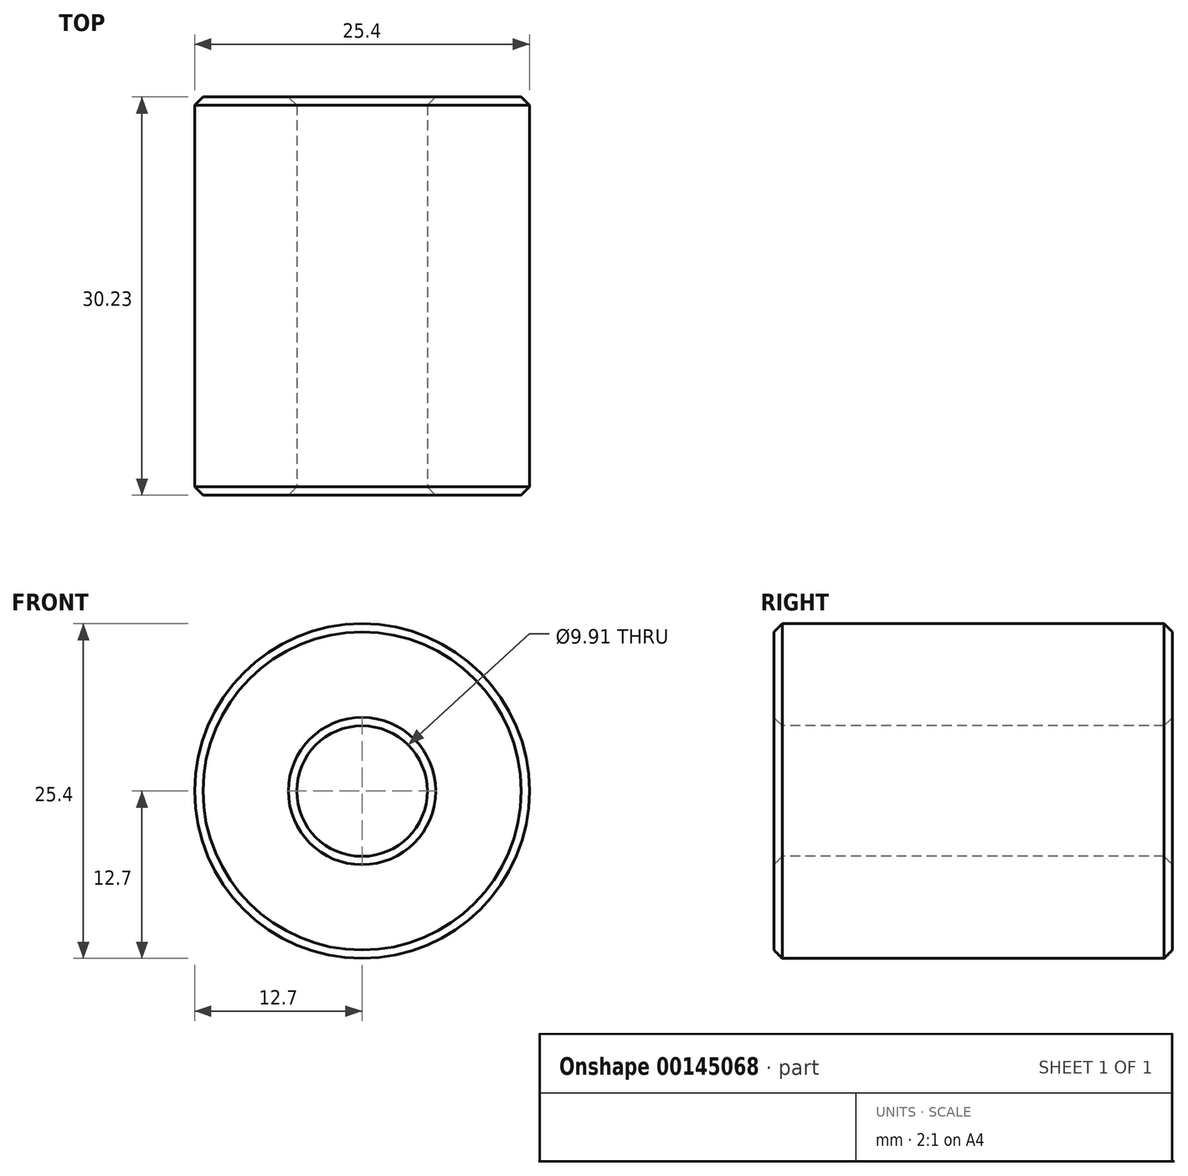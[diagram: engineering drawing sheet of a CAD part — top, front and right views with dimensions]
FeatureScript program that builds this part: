
annotation { "Feature Type Name" : "Feature", "Feature Type Description" : "" }
export const myFeature = defineFeature(function(context is Context, id is Id, definition is map)
    precondition{}
    {
        {
            var Q0;
            Q0=qCreatedBy(makeId("Front.planeOp"),FACE);
            var sketch = newSketch(context, id + "F0", { "sketchPlane" : qUnion([Q0])});
            skCircle(sketch, "E0", {"center": v(0, 0) * mm, "radius": 12.7 * mm});
            skCircle(sketch, "E1", {"center": v(0, 0) * mm, "radius": 4.95 * mm});
            skSolve(sketch);
        }
        {
            var Q0;
            Q0=makeQuery(id+"F0.imprint","IMPRINT",FACE,{"disambiguationData":[TD([[makeQuery(id+"F0.imprint","IMPRINT",EDGE,{"derivedFrom":sQuery(id+"F0.wireOp",EDGE,"E0")}),1.0]])]});
            extrude(context, id + "F1", {"entities" : qUnion([Q0]), "oppositeDirection" : true, "depth" : 30.23 * mm});
        }
        {
            var Q0;
            Q0=makeQuery(id+"F1.opExtrude","CAP_EDGE",EDGE,{"disambiguationData":[OSD([sQuery(id+"F0.wireOp",EDGE,"E0")])],"isStart":true});
            var Q1;
            Q1=makeQuery(id+"F1.opExtrude","CAP_EDGE",EDGE,{"disambiguationData":[OSD([sQuery(id+"F0.wireOp",EDGE,"E1")])],"isStart":true});
            var Q2;
            Q2=makeQuery(id+"F1.opExtrude","CAP_EDGE",EDGE,{"disambiguationData":[OSD([sQuery(id+"F0.wireOp",EDGE,"E0")])],"isStart":false});
            var Q3;
            Q3=makeQuery(id+"F1.opExtrude","CAP_EDGE",EDGE,{"disambiguationData":[OSD([sQuery(id+"F0.wireOp",EDGE,"E1")])],"isStart":false});
            chamfer(context, id + "F2", {"entities" : qUnion([Q0, Q1, Q2, Q3]), "width" : 0.64 * mm, "tangentPropagation" : true});
        }
    });
